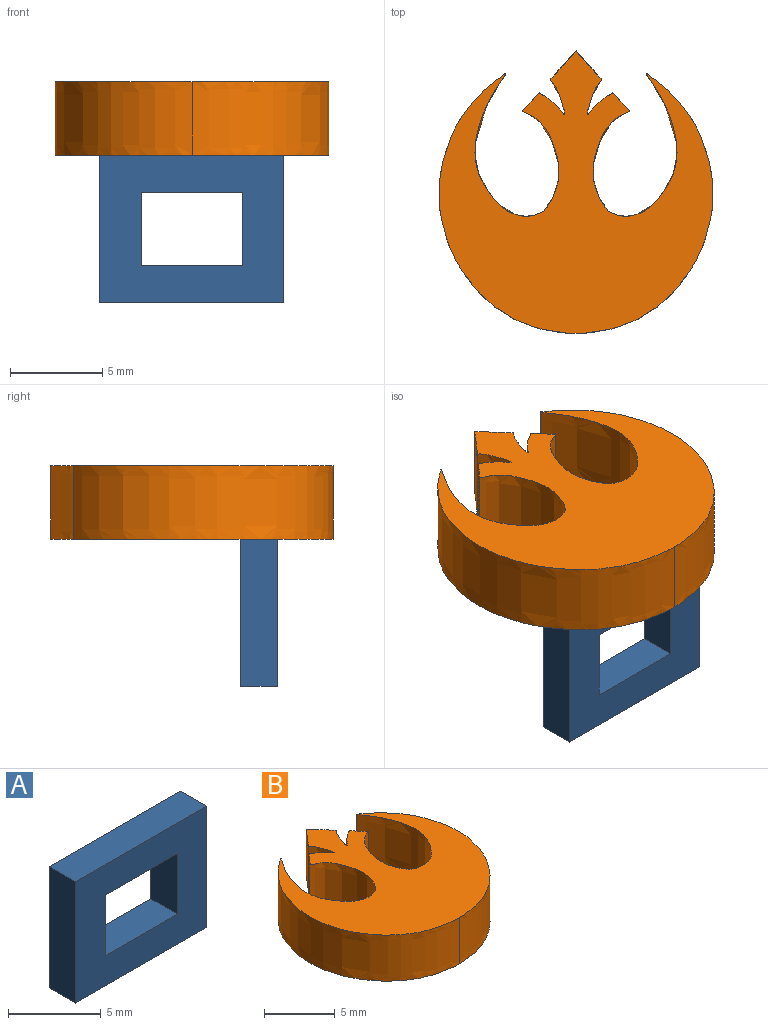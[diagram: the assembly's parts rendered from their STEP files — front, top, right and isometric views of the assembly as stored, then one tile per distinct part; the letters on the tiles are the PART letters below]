
ASSEMBLY  parts=2 mates=1
PART A: 10 faces, bbox 10x2x8 mm
  f0: plane 10x8mm, normal (0,-1,0), area 58mm2, adj f1,f3,f4,f5,f6,f7,f8,f9
  f1: plane 8x2mm, normal (1,0,0), area 16mm2, adj f0,f2,f4,f5
  f2: plane 10x8mm, normal (0,1,0), area 58mm2, adj f1,f3,f4,f5,f6,f7,f8,f9
  f3: plane 8x2mm, normal (-1,0,0), area 16mm2, adj f0,f2,f4,f5
  f4: plane 10x2mm, normal (0,0,-1), area 20mm2, adj f0,f1,f2,f3
  f5: plane 10x2mm, normal (0,0,1), area 20mm2, adj f0,f1,f2,f3
  f6: plane 5.5x2mm, normal (0,0,-1), area 11mm2, adj f0,f2,f7,f9
  f7: plane 4x2mm, normal (1,0,0), area 8mm2, adj f0,f2,f6,f8
  f8: plane 5.5x2mm, normal (0,0,1), area 11mm2, adj f0,f2,f7,f9
  f9: plane 4x2mm, normal (-1,0,0), area 8mm2, adj f0,f2,f6,f8
PART B: 4 faces, bbox 14.9x15.4x4 mm
  f0: extruded ~15.34x7.42mm, area 183.9mm2, adj f1,f2,f3
  f1: extruded ~15.34x7.42mm, area 183.9mm2, adj f0,f2,f3
  f2: plane 15.35x14.86mm, normal (0,0,1), area 119.5mm2, adj f0,f1
  f3: plane 15.35x14.86mm, normal (0,0,-1), area 119.5mm2, adj f0,f1
PLACE A t=(0.14,-2.84,-0.94)mm
PLACE B t=(0.15,0.62,-0.94)mm fixed
MATE planar A.f5 <-> B.f3  axis (0,0,1) through (0.14,-2.84,-0.94)mm
